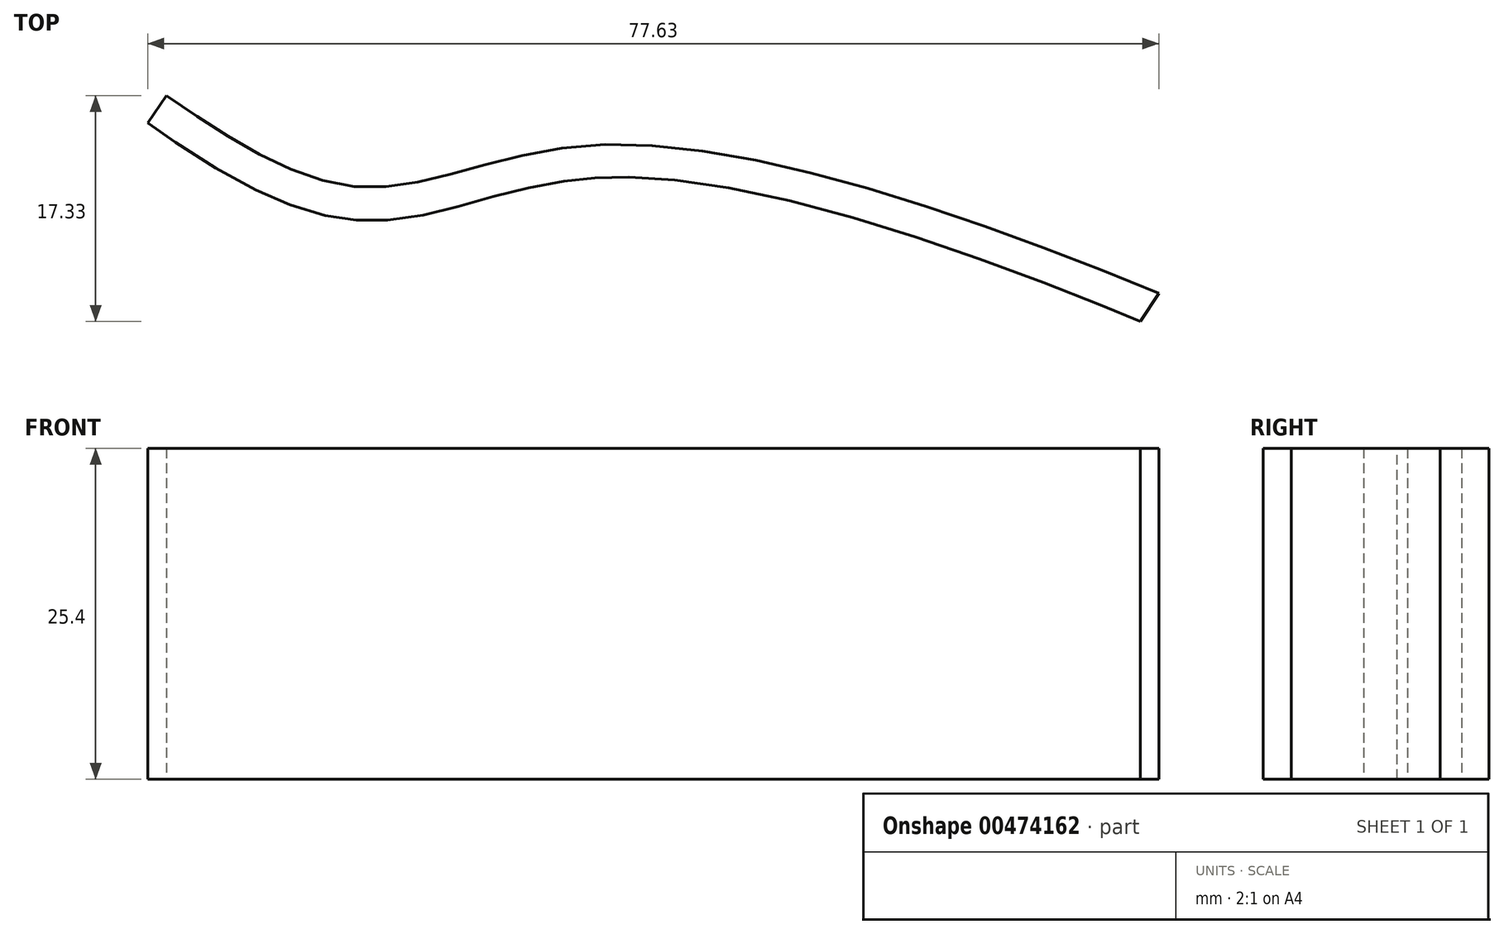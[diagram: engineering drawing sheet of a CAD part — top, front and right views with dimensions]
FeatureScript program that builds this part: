
annotation { "Feature Type Name" : "Feature", "Feature Type Description" : "" }
export const myFeature = defineFeature(function(context is Context, id is Id, definition is map)
    precondition{}
    {
        {
            var Q0;
            Q0=qCreatedBy(makeId("Top.planeOp"),FACE);
            var sketch = newSketch(context, id + "F0", { "sketchPlane" : qUnion([Q0])});
            skFitSpline(sketch, "E0", {"points": [v(0, 0) * mm, v(14.98, -7.02) * mm, v(32.8, -3.8) * mm, v(76.2, -15.17) * mm], "startDerivative": vector(53.88, -36.77) * mm, "endDerivative": vector(99.65, -40.9) * mm});
            skFitSpline(sketch, "E1.0", {"points": [v(-1.43, -2.1) * mm, v(-0.3, -2.87) * mm, v(2, -4.43) * mm, v(5, -6.27) * mm, v(7.5, -7.54) * mm, v(9.42, -8.36) * mm, v(11.4, -9.01) * mm, v(13.1, -9.38) * mm, v(14.49, -9.54) * mm, v(15.89, -9.6) * mm, v(17.59, -9.5) * mm, v(19.56, -9.2) * mm, v(21.49, -8.75) * mm, v(23.4, -8.23) * mm, v(25.3, -7.7) * mm, v(27.25, -7.2) * mm, v(29.25, -6.76) * mm, v(30.99, -6.5) * mm, v(32.43, -6.35) * mm, v(33.92, -6.27) * mm, v(35.9, -6.28) * mm, v(39.3, -6.5) * mm, v(43.9, -7.2) * mm, v(49.88, -8.58) * mm, v(56.13, -10.4) * mm, v(62.54, -12.58) * mm, v(68.97, -14.98) * mm, v(73.17, -16.67) * mm, v(75.24, -17.52) * mm]});
            skLineSegment(sketch, "E2", {"start": v(0, 0) * mm, "end": v(-1.43, -2.1) * mm});
            skLineSegment(sketch, "E3", {"start": v(76.2, -15.17) * mm, "end": v(74.77, -17.33) * mm});
            skSolve(sketch);
        }
        {
            var Q0;
            Q0=makeQuery(id+"F0.imprint","IMPRINT",FACE,{"disambiguationData":[TD([[makeQuery(id+"F0.imprint","IMPRINT",EDGE,{"derivedFrom":sQuery(id+"F0.wireOp",EDGE,"E0")}),-1.0]])]});
            extrude(context, id + "F1", {"entities" : qUnion([Q0]), "depth" : 25.4 * mm});
        }
    });
